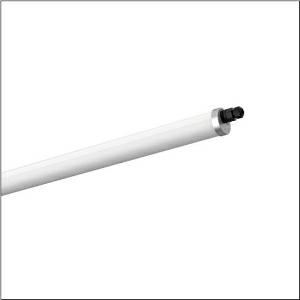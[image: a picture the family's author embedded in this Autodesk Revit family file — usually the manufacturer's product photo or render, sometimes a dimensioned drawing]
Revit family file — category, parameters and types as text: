
# Revit family: monsun_r__31_tube_51ft10dn460a_a449
name_source: partatom
category: Lighting Fixtures
units: mm (PartAtom-declared; Revit-internal decimal feet)

## family parameters
Cut with Voids When Loaded = No
Host = Face
Light Source = No
Part Type = Normal
Room Calculation Point = No
Round Connector Dimension = Use Diameter
Shared = No

## types (1)
- Monsun® 31 Tube (1 x LED, 6500 lm, 40 W, 4000K)
    Apparent Load = 40 VA
    CIE Flux Codes = 42 71 90 91 100
    Color Rendering = 80
    Color Temperature = 4000K
    Default Elevation = 1800 mm
    Description = Monsun® 31 Tube, tubular luminaire, primary optical cover: diffuser, of PMMA, light emission: direct distribution, primary light characteristic: symmetric, installation type: suspended mounting, surface-mounted, LED, rated luminous flux: 6.500lm, luminous efficacy: 160lm/W, light colour: 840, colour temperature: 4000K, control gear: DALI 2, with with 1 terminal, 5-pole, max. 2.5mm², through-wiring: 5x 1.5mm², mains connection: 220..240V, AC, 50/60Hz, rated input power: 40W, housing, cylindrical, of PMMA, semi-transparent, matt white, with luminaire and ceiling fastening, V4A, mounting with brackets of stainless steel, length: 1.570mm, diameter: 75mm, end cap, of stainless steel (V4A), protection rating (complete): IP67/IP69K, insulation class (complete): insulation class I (protective earthing), certification: CE, UKCA, impact resistance: IK07, permissible operating ambient temperature: -20..+40°C, corresponds to IFS (International Featured Standards) requirements for safety and quality in the food industry, usage in unprotected outdoor areas possible with horizontal mounting, contact your sales advisor before using the luminaires in applications with unclear chemical exposure, large temperature fluctuations or condensation-forming humidity, packaging unit: 1 piece
    Height = 83 mm
    Lamp = 1 x LED
    Lamp Light Flux = 6500 lm
    Lamp Power = 40 W
    Lamp count = 1
    Length = 1570 mm
    Luminous efficacy = 163 lm/W
    Manufacturer = Siteco
    ModVariant = No
    Model = 51FT10DN460A
    Mounting Place = Ceiling
    Mounting Type = Pendant
    Number of Poles = 1
    OnlyDefault = Yes
    Power Factor = 1
    Product Name = Monsun® 31 Tube
    Product group = tubular luminaire
    ProductGroupID = 907
    Protection Class = Protection class I
    RLX_Detail_Level = 1
    RLX_Emergency_Light_Flux = 0 lm
    RLX_Emergency_Type = 0
    RLX_Emergency_Type_DB = No
    RlxData = <blob elided: 25309 chars, md5=f96b861d>
    Socket = socket
    Standby Power = 0 W
    System Light Flux = 6500 lm
    System Power = 40 W
    Type Comments = Product without accessories
    Type Image = l_1228461.jpg
    URL = http://relux.com
    VarID = ---
    Voltage = 0 V
    Weight = 0.00 kg
    Width = 75 mm

## geometry (parser evidence)
native form markers: Blend x4, Sweep x14
no freeform markers — native parametric forms only
